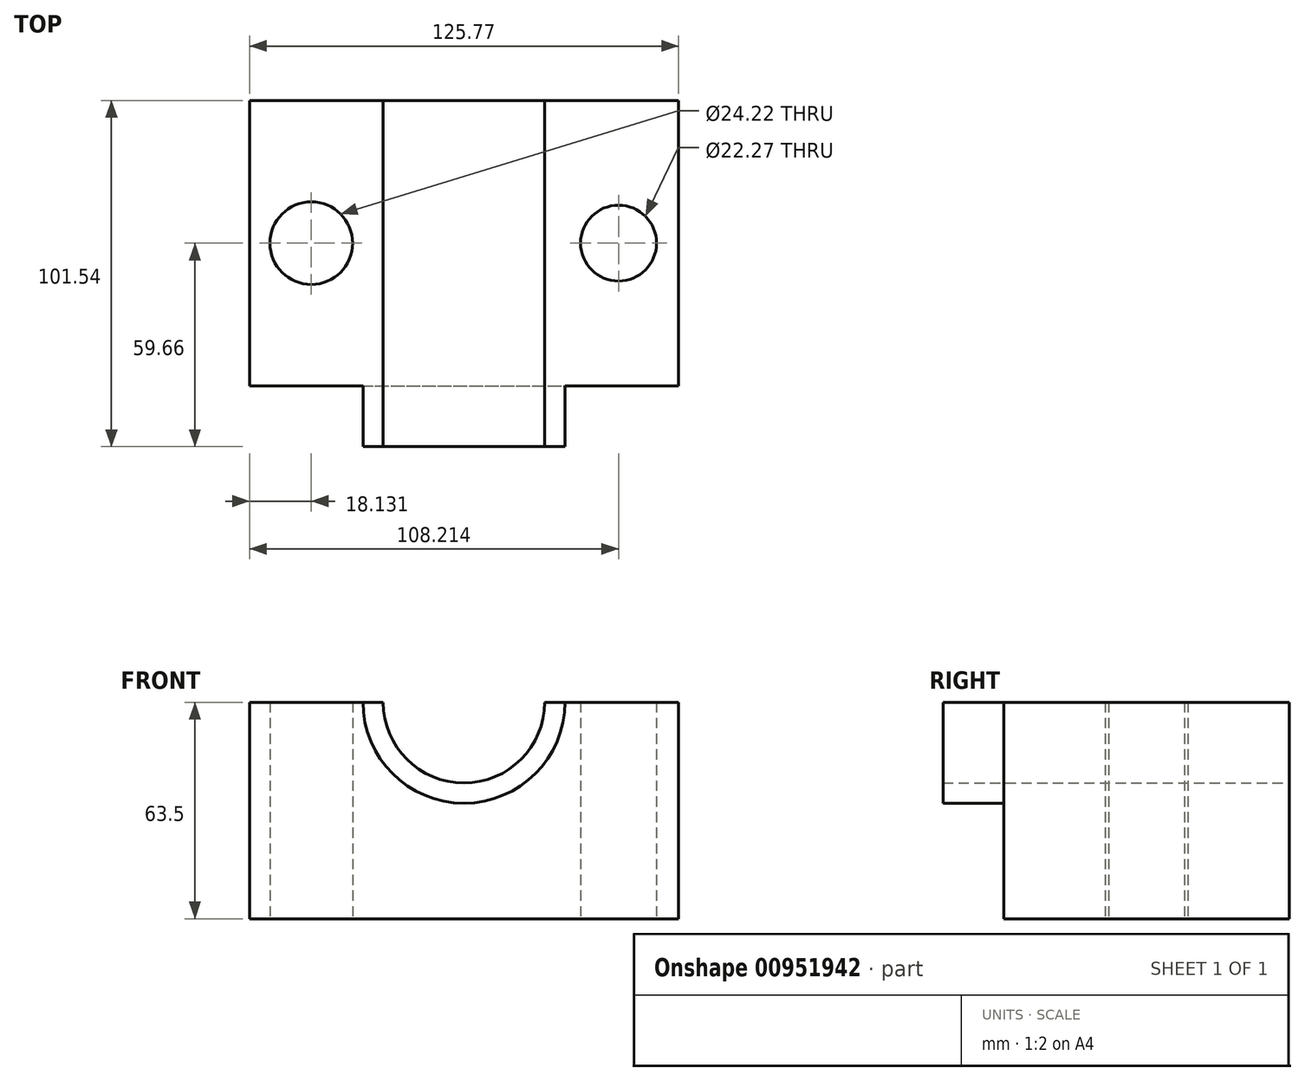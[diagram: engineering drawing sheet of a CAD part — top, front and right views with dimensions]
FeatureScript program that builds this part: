
annotation { "Feature Type Name" : "Feature", "Feature Type Description" : "" }
export const myFeature = defineFeature(function(context is Context, id is Id, definition is map)
    precondition{}
    {
        {
            var Q0;
            Q0=qCreatedBy(makeId("Top.planeOp"),FACE);
            var sketch = newSketch(context, id + "F0", { "sketchPlane" : qUnion([Q0])});
            skLineSegment(sketch, "E0.bottom", {"start": v(-63.46, 41.88) * mm, "end": v(62.3, 41.88) * mm});
            skLineSegment(sketch, "E0.top", {"start": v(-63.46, -41.88) * mm, "end": v(62.3, -41.88) * mm});
            skLineSegment(sketch, "E0.left", {"start": v(-63.46, 41.88) * mm, "end": v(-63.46, -41.88) * mm});
            skLineSegment(sketch, "E0.right", {"start": v(62.3, 41.88) * mm, "end": v(62.3, -41.88) * mm});
            skCircle(sketch, "E1", {"center": v(-45.33, 0) * mm, "radius": 12.1 * mm});
            skCircle(sketch, "E2", {"center": v(44.75, 0) * mm, "radius": 11.14 * mm});
            skSolve(sketch);
        }
        {
            var Q0;
            Q0=makeQuery(id+"F0.imprint","IMPRINT",FACE,{"disambiguationData":[TD([[makeQuery(id+"F0.imprint","IMPRINT",EDGE,{"derivedFrom":sQuery(id+"F0.wireOp",EDGE,"E0.bottom")}),-1.0]])]});
            extrude(context, id + "F1", {"entities" : qUnion([Q0]), "depth" : 63.5 * mm, "offsetDistance" : 25.4 * mm});
        }
        {
            var Q0;
            Q0=makeQuery(id+"F1.opExtrude","SWEPT_FACE",FACE,{"disambiguationData":[OSD([sQuery(id+"F0.wireOp",EDGE,"E0.top")])]});
            var sketch = newSketch(context, id + "F2", { "sketchPlane" : qUnion([Q0])});
            skCircle(sketch, "E3", {"center": v(-0.58, 63.5) * mm, "radius": 23.67 * mm});
            skCircle(sketch, "E4", {"center": v(-0.58, 63.5) * mm, "radius": 29.6 * mm});
            skSolve(sketch);
        }
        {
            var Q0;
            {var subQ0=sQuery(id+"F2.wireOp",EDGE,"E3");var subQ1=makeQuery(id+"F1.opExtrude","CAP_EDGE",EDGE,{"disambiguationData":[OSD([sQuery(id+"F0.wireOp",EDGE,"E0.top")])],"isStart":false});var subQ2=makeQuery(id+"F2.imprint","INTERSECT",VERTEX,{"disambiguationData":[OD(0.0)],"derivedFrom":[subQ1,subQ0]});Q0=makeQuery(id+"F2.imprint","IMPRINT",FACE,{"disambiguationData":[TD([[makeQuery(id+"F2.imprint","IMPRINT",EDGE,{"disambiguationData":[TD([[subQ2,-1.0]])],"derivedFrom":subQ0}),-1.0]])]});}
            extrude(context, id + "F3", {"entities" : qUnion([Q0]), "operationType" : NewBodyOperationType.ADD, "depth" : 17.78 * mm, "offsetDistance" : 25.4 * mm});
        }
        {
            var Q0;
            {var subQ0=sQuery(id+"F0.wireOp",EDGE,"E0.top");var subQ3=sQuery(id+"F2.wireOp",EDGE,"E3");Q0=makeQuery(id+"F3.boolean.opBoolean","SPLIT",FACE,{"disambiguationData":[TD([makeQuery(id+"F3.opExtrude","SWEPT_FACE",FACE,{"disambiguationData":[OSD([subQ3])]})])],"derivedFrom":makeQuery(id+"F1.opExtrude","SWEPT_FACE",FACE,{"disambiguationData":[OSD([subQ0])]})});}
            extrude(context, id + "F4", {"entities" : qUnion([Q0]), "operationType" : NewBodyOperationType.REMOVE, "oppositeDirection" : true, "depth" : 98.04 * mm, "offsetDistance" : 25.4 * mm});
        }
    });
